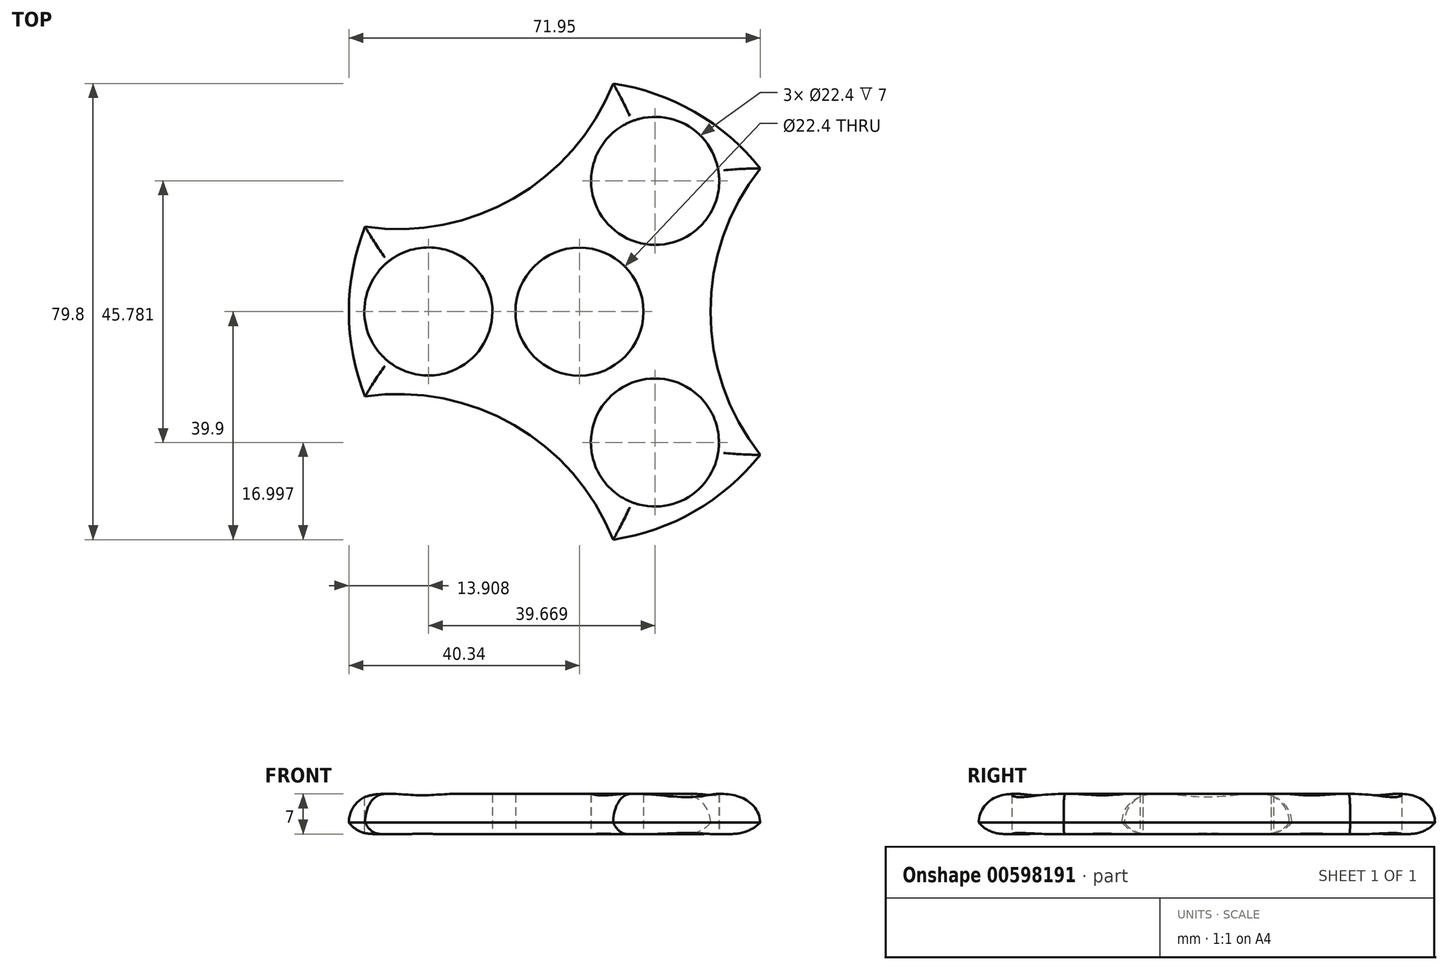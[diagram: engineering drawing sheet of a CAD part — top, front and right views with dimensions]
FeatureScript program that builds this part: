
annotation { "Feature Type Name" : "Feature", "Feature Type Description" : "" }
export const myFeature = defineFeature(function(context is Context, id is Id, definition is map)
    precondition{}
    {
        {
            var Q0;
            Q0=qCreatedBy(makeId("Top.planeOp"),FACE);
            var sketch = newSketch(context, id + "F0", { "sketchPlane" : qUnion([Q0])});
            skCircle(sketch, "E0", {"center": v(0, 0) * mm, "radius": 11.2 * mm});
            skArc(sketch, "E1", {"start": v(31.6, 25.06) * mm, "mid": v(20.17, 34.93) * mm, "end": v(5.9, 39.9) * mm});
            skArc(sketch, "E2", {"start": v(31.6, 25.06) * mm, "mid": v(22.9, 0) * mm, "end": v(31.6, -25.06) * mm});
            skArc(sketch, "E3.1.0", {"start": v(-37.5, 14.85) * mm, "mid": v(-11.45, 19.84) * mm, "end": v(5.9, 39.9) * mm});
            skArc(sketch, "E3.2.0", {"start": v(5.9, -39.9) * mm, "mid": v(-11.45, -19.84) * mm, "end": v(-37.5, -14.85) * mm});
            skArc(sketch, "E4.trimOffspring", {"start": v(5.9, -39.9) * mm, "mid": v(20.17, -34.93) * mm, "end": v(31.6, -25.06) * mm});
            skArc(sketch, "E5.trimOffspring", {"start": v(-37.5, 14.85) * mm, "mid": v(-40.34, 0) * mm, "end": v(-37.5, -14.85) * mm});
            skPoint(sketch, "E6.center.orphan", {"position": v(0, -29.72) * mm});
            skCircle(sketch, "E7", {"center": v(13.24, 22.88) * mm, "radius": 11.2 * mm});
            skCircle(sketch, "E8.1.0", {"center": v(-26.43, 0.03) * mm, "radius": 11.2 * mm});
            skCircle(sketch, "E8.2.0", {"center": v(13.2, -22.9) * mm, "radius": 11.2 * mm});
            skSolve(sketch);
        }
        {
            var Q0;
            Q0 = qSketchRegion(id + "F0", true);
            extrude(context, id + "F1", {"entities" : qUnion([Q0]), "depth" : 7 * mm, "offsetDistance" : 25 * mm});
        }
        {
            var Q0;
            Q0=makeQuery(id+"F1.opExtrude","CAP_EDGE",EDGE,{"disambiguationData":[OSD([sQuery(id+"F0.wireOp",EDGE,"E2")])],"isStart":false});
            var Q1;
            Q1=makeQuery(id+"F1.opExtrude","CAP_EDGE",EDGE,{"disambiguationData":[OSD([sQuery(id+"F0.wireOp",EDGE,"E1")])],"isStart":false});
            var Q2;
            Q2=makeQuery(id+"F1.opExtrude","CAP_EDGE",EDGE,{"disambiguationData":[OSD([sQuery(id+"F0.wireOp",EDGE,"E3.2.0")])],"isStart":false});
            var Q3;
            Q3=makeQuery(id+"F1.opExtrude","CAP_EDGE",EDGE,{"disambiguationData":[OSD([sQuery(id+"F0.wireOp",EDGE,"E4.trimOffspring")])],"isStart":false});
            var Q4;
            Q4=makeQuery(id+"F1.opExtrude","CAP_EDGE",EDGE,{"disambiguationData":[OSD([sQuery(id+"F0.wireOp",EDGE,"E5.trimOffspring")])],"isStart":false});
            var Q5;
            Q5=makeQuery(id+"F1.opExtrude","CAP_EDGE",EDGE,{"disambiguationData":[OSD([sQuery(id+"F0.wireOp",EDGE,"E3.1.0")])],"isStart":false});
            fillet(context, id + "F2", {"entities" : qUnion([Q0, Q1, Q2, Q3, Q4, Q5]), "radius" : 5 * mm, "tangentPropagation" : true, "allowEdgeOverflow" : false});
        }
        {
            var Q0;
            Q0=makeQuery(id+"F1.opExtrude","CAP_EDGE",EDGE,{"disambiguationData":[OSD([sQuery(id+"F0.wireOp",EDGE,"E3.2.0")])],"isStart":true});
            var Q1;
            Q1=makeQuery(id+"F1.opExtrude","CAP_EDGE",EDGE,{"disambiguationData":[OSD([sQuery(id+"F0.wireOp",EDGE,"E5.trimOffspring")])],"isStart":true});
            var Q2;
            Q2=makeQuery(id+"F1.opExtrude","CAP_EDGE",EDGE,{"disambiguationData":[OSD([sQuery(id+"F0.wireOp",EDGE,"E3.1.0")])],"isStart":true});
            var Q3;
            Q3=makeQuery(id+"F1.opExtrude","CAP_EDGE",EDGE,{"disambiguationData":[OSD([sQuery(id+"F0.wireOp",EDGE,"E1")])],"isStart":true});
            var Q4;
            Q4=makeQuery(id+"F1.opExtrude","CAP_EDGE",EDGE,{"disambiguationData":[OSD([sQuery(id+"F0.wireOp",EDGE,"E2")])],"isStart":true});
            var Q5;
            Q5=makeQuery(id+"F1.opExtrude","CAP_EDGE",EDGE,{"disambiguationData":[OSD([sQuery(id+"F0.wireOp",EDGE,"E4.trimOffspring")])],"isStart":true});
            fillet(context, id + "F3", {"entities" : qUnion([Q0, Q1, Q2, Q3, Q4, Q5]), "radius" : 5 * mm, "tangentPropagation" : true, "allowEdgeOverflow" : false});
        }
    });
